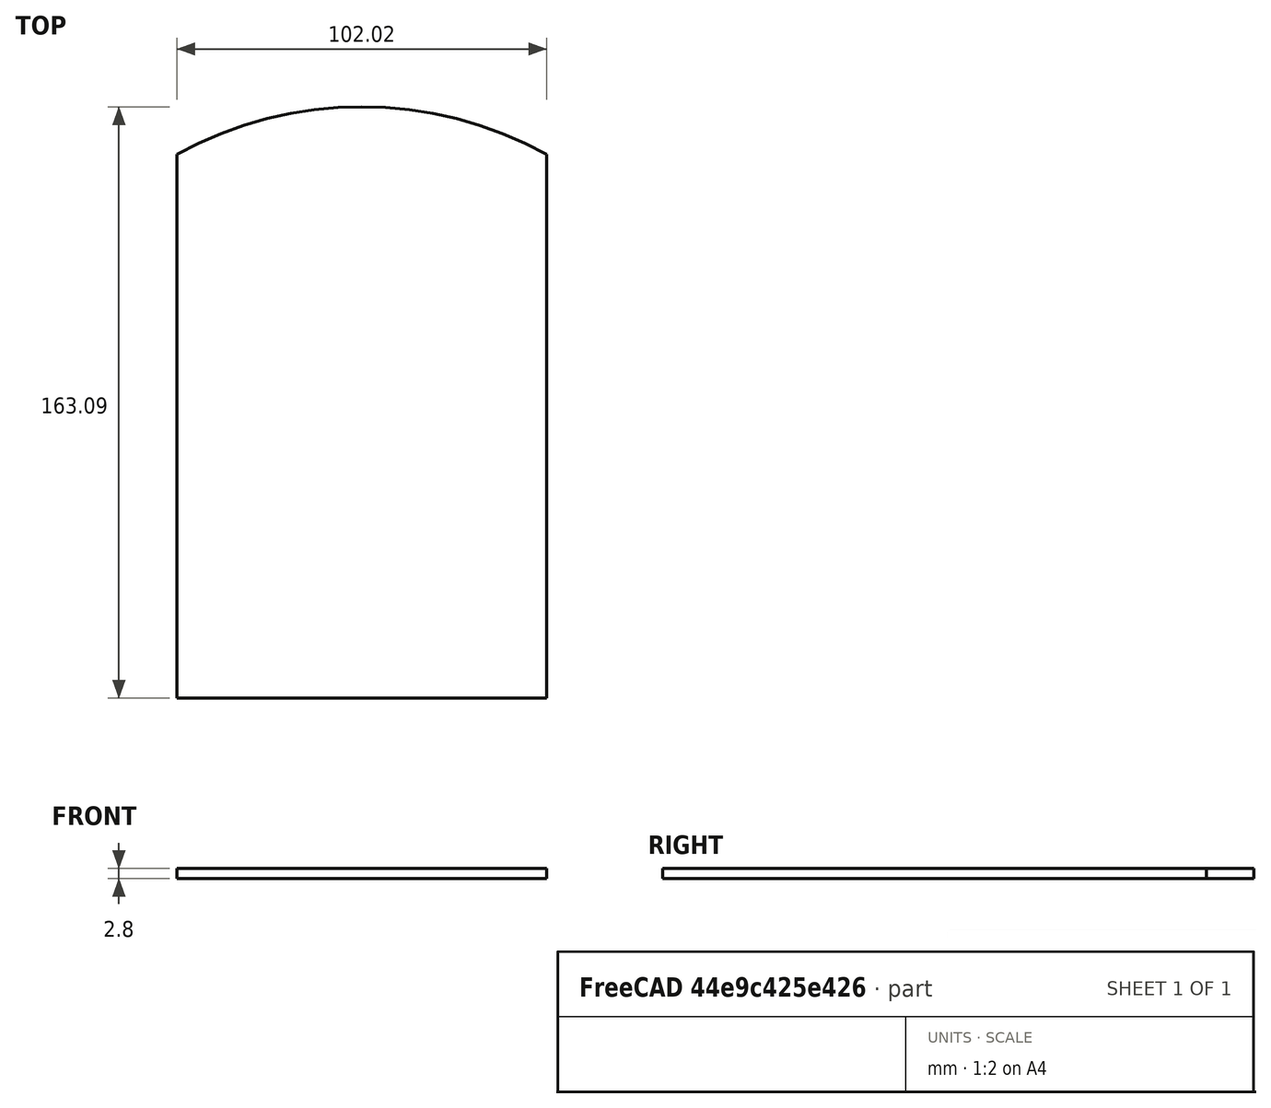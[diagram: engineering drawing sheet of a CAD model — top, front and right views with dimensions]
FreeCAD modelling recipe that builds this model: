
FCSTD DOCUMENT  (FreeCAD 0.16R6704 (Git))
Label: segundo piso
License: All rights reserved
LicenseURL: http://en.wikipedia.org/wiki/All_rights_reserved
objects: Sketcher::SketchObject×1, PartDesign::Pad×1
note: 3 computed .brp shape members not serialized (recipe doc carries the construction recipe); baked Part::Feature solids carry a one-line shape summary decoded from their .brp

FEATURE [Sketcher::SketchObject] Sketch001
  sketch-geometry (13):
    g0: GeomPoint [constr] X=2.73482e-06 Y=-64.9838 Z=0
    g1: GeomPoint [constr] X=0.000781089 Y=-94.5802 Z=0
    g2: GeomPoint [constr] X=5.17953e-06 Y=-94.5802 Z=0
    g3: ArcOfCircle CenterX=0 CenterY=0 CenterZ=0 NormalX=0 NormalY=0 NormalZ=1 Radius=105.941 StartAngle=1.06846 EndAngle=2.07313
    g4: LineSegment StartX=51.0075 StartY=92.8534 StartZ=0 EndX=51.0075 EndY=-0.146646 EndZ=0
    g5: LineSegment StartX=51.0075 StartY=-13.1466 StartZ=0 EndX=51.0075 EndY=-57.1466 EndZ=0
    g6: LineSegment StartX=-51.0075 StartY=92.8534 StartZ=0 EndX=-51.0075 EndY=-0.146646 EndZ=0
    g7: LineSegment StartX=-51.0075 StartY=-57.1466 StartZ=0 EndX=-51.0075 EndY=-13.1466 EndZ=0
    g8: GeomPoint [constr] X=0 Y=12.0048 Z=0
    g9: GeomPoint [constr] X=0 Y=31.9888 Z=0
    g10: LineSegment StartX=-51.0075 StartY=-57.1466 StartZ=0 EndX=51.0075 EndY=-57.1466 EndZ=0
    g11: LineSegment StartX=-51.0075 StartY=-0.146646 StartZ=0 EndX=-51.0075 EndY=-13.1466 EndZ=0
    g12: LineSegment StartX=51.0075 StartY=-0.146646 StartZ=0 EndX=51.0075 EndY=-13.1466 EndZ=0
  constraints (25):
    c: Coincident(g3,g-1)
    c: Vertical(g4)
    c: Distance(g4,g4) = 93
    c: Distance(g5,g4) = 13
    c: Vertical(g5)
    c: Vertical(g6)
    c: Distance(g3,g6) = 93
    c: Distance(g6,g7) = 13
    c: Vertical(g7)
    c: Coincident(g4,g3)
    c: Coincident(g6,g3)
    c: PointOnObject(g8,g-2)
    c: PointOnObject(g9,g-2)
    c: Horizontal(g10)
    c: Coincident(g11,g6)
    c: Coincident(g11,g7)
    c: Vertical(g11)
    c: Coincident(g12,g4)
    c: Coincident(g12,g5)
    c: Vertical(g12)
    c: Distance(g3,g5) = 150
    c: Distance(g7,g3) = 150
    c: Distance(g3,g3) = 102.015
    c: Coincident(g5,g10)
    c: Coincident(g7,g10)
FEATURE [PartDesign::Pad] Pad
  Length = 2.8
  Length2 = 100
  Sketch = -> Sketch001
  Type = 0
